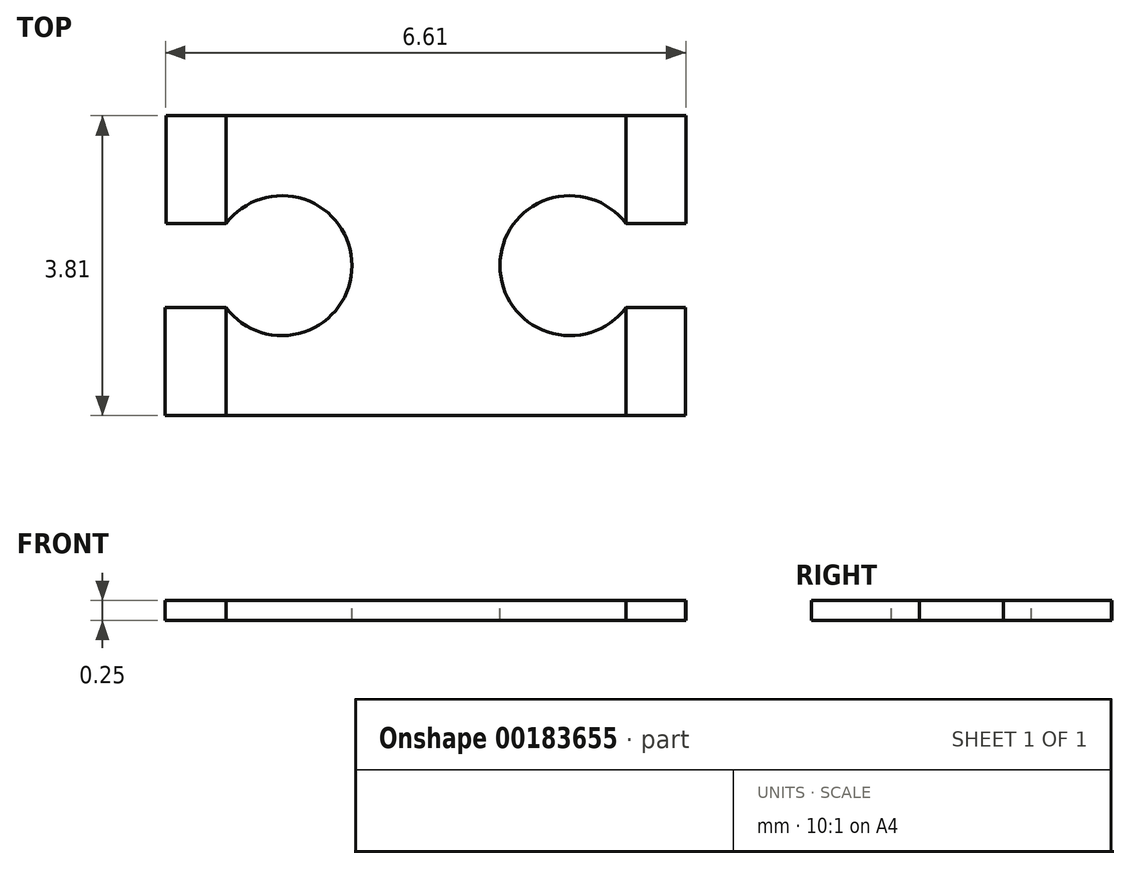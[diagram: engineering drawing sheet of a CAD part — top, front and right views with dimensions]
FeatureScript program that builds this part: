
annotation { "Feature Type Name" : "Feature", "Feature Type Description" : "" }
export const myFeature = defineFeature(function(context is Context, id is Id, definition is map)
    precondition{}
    {
        {
            var Q0;
            Q0=qCreatedBy(makeId("Top.planeOp"),FACE);
            var sketch = newSketch(context, id + "F0", { "sketchPlane" : qUnion([Q0])});
            skLineSegment(sketch, "E0.bottom", {"start": v(0, 0) * mm, "end": v(-5.08, 0) * mm});
            skLineSegment(sketch, "E0.top", {"start": v(0, 3.8) * mm, "end": v(-5.08, 3.8) * mm});
            skLineSegment(sketch, "E0.left", {"start": v(0, 0) * mm, "end": v(0, 3.8) * mm});
            skLineSegment(sketch, "E0.right", {"start": v(-5.08, 0) * mm, "end": v(-5.08, 3.8) * mm});
            skSolve(sketch);
        }
        {
            var Q0;
            Q0 = qSketchRegion(id + "F0", true);
            var Q1;
            Q1 = qSketchRegion(id + "F2", true);
            extrude(context, id + "F1", {"entities" : qUnion([Q0, Q1]), "depth" : 0.25 * mm});
        }
        {
            var Q0;
            Q0=makeQuery(id+"F1.opExtrude","CAP_FACE",FACE,{"disambiguationData":[OSD([sQuery(id+"F0.wireOp",EDGE,"E0.bottom"),sQuery(id+"F0.wireOp",EDGE,"E0.top"),sQuery(id+"F0.wireOp",EDGE,"E0.left"),sQuery(id+"F0.wireOp",EDGE,"E0.right")])],"isStart":false});
            var sketch = newSketch(context, id + "F2", { "sketchPlane" : qUnion([Q0])});
            skLineSegment(sketch, "E1", {"start": v(-5.08, 1.9) * mm, "end": v(-4.37, 1.9) * mm});
            skSolve(sketch);
        }
        {
            var Q0;
            Q0=sQuery(id+"F2.wireOp",VERTEX,"E1.end");
            var Q1;
            Q1=makeQuery(id+"F1.opExtrude","SWEPT_BODY",BODY,{"disambiguationData":[OSD([sQuery(id+"F0.wireOp",EDGE,"E0.bottom"),sQuery(id+"F0.wireOp",EDGE,"E0.top"),sQuery(id+"F0.wireOp",EDGE,"E0.left"),sQuery(id+"F0.wireOp",EDGE,"E0.right")])]});
            hole(context, id + "F3", {"style" : HoleStyle.SIMPLE, "endStyle" : HoleEndStyle.BLIND, "holeDiameter" : 1.78 * mm, "holeDepth" : 25.4 * mm, "locations" : qUnion([Q0]), "scope" : qUnion([Q1])});
        }
        {
            var Q0;
            Q0=makeQuery(id+"F1.opExtrude","CAP_FACE",FACE,{"disambiguationData":[OSD([sQuery(id+"F0.wireOp",EDGE,"E0.bottom"),sQuery(id+"F0.wireOp",EDGE,"E0.top"),sQuery(id+"F0.wireOp",EDGE,"E0.left"),sQuery(id+"F0.wireOp",EDGE,"E0.right")])],"isStart":false});
            var sketch = newSketch(context, id + "F4", { "sketchPlane" : qUnion([Q0])});
            skLineSegment(sketch, "E2", {"start": v(0, 1.9) * mm, "end": v(-0.71, 1.9) * mm});
            skSolve(sketch);
        }
        {
            var Q0;
            Q0=sQuery(id+"F4.wireOp",VERTEX,"E2.end");
            var Q1;
            Q1=makeQuery(id+"F1.opExtrude","SWEPT_BODY",BODY,{"disambiguationData":[OSD([sQuery(id+"F0.wireOp",EDGE,"E0.bottom"),sQuery(id+"F0.wireOp",EDGE,"E0.top"),sQuery(id+"F0.wireOp",EDGE,"E0.left"),sQuery(id+"F0.wireOp",EDGE,"E0.right")])]});
            hole(context, id + "F5", {"style" : HoleStyle.SIMPLE, "endStyle" : HoleEndStyle.BLIND, "holeDiameter" : 1.78 * mm, "holeDepth" : 25.4 * mm, "locations" : qUnion([Q0]), "scope" : qUnion([Q1])});
        }
        {
            var Q0;
            Q0=makeQuery(id+"F1.opExtrude","CAP_FACE",FACE,{"disambiguationData":[OSD([sQuery(id+"F0.wireOp",EDGE,"E0.bottom"),sQuery(id+"F0.wireOp",EDGE,"E0.top"),sQuery(id+"F0.wireOp",EDGE,"E0.left"),sQuery(id+"F0.wireOp",EDGE,"E0.right")])],"isStart":false});
            var sketch = newSketch(context, id + "F6", { "sketchPlane" : qUnion([Q0])});
            skLineSegment(sketch, "E3", {"start": v(-5.08, 2.44) * mm, "end": v(-5.84, 2.44) * mm});
            skLineSegment(sketch, "E4", {"start": v(-5.08, 3.8) * mm, "end": v(-5.84, 3.8) * mm});
            skLineSegment(sketch, "E5", {"start": v(-5.84, 3.8) * mm, "end": v(-5.84, 2.44) * mm});
            skLineSegment(sketch, "E6", {"start": v(-5.08, 1.37) * mm, "end": v(-5.84, 1.37) * mm});
            skLineSegment(sketch, "E7", {"start": v(-5.84, 1.37) * mm, "end": v(-5.84, 0) * mm});
            skLineSegment(sketch, "E8", {"start": v(-5.84, 0) * mm, "end": v(-5.08, 0) * mm});
            skLineSegment(sketch, "E9", {"start": v(0, 2.44) * mm, "end": v(0.76, 2.44) * mm});
            skLineSegment(sketch, "E10", {"start": v(0, 3.8) * mm, "end": v(0.76, 3.8) * mm});
            skLineSegment(sketch, "E11", {"start": v(0.76, 3.8) * mm, "end": v(0.76, 2.44) * mm});
            skLineSegment(sketch, "E12", {"start": v(0, 1.37) * mm, "end": v(0.76, 1.37) * mm});
            skLineSegment(sketch, "E13", {"start": v(0.76, 1.37) * mm, "end": v(0.76, 0) * mm});
            skLineSegment(sketch, "E14", {"start": v(0.76, 0) * mm, "end": v(0, 0) * mm});
            skSolve(sketch);
        }
        {
            var Q0;
            Q0=makeQuery(id+"F6.imprint","IMPRINT",FACE,{"disambiguationData":[TD([[makeQuery(id+"F6.imprint","IMPRINT",EDGE,{"derivedFrom":sQuery(id+"F6.wireOp",EDGE,"E9")}),1.0]])]});
            extrude(context, id + "F7", {"entities" : qUnion([Q0]), "oppositeDirection" : true, "depth" : 0.25 * mm});
        }
        {
            var Q0;
            Q0=makeQuery(id+"F1.opExtrude","CAP_FACE",FACE,{"disambiguationData":[OSD([sQuery(id+"F0.wireOp",EDGE,"E0.bottom"),sQuery(id+"F0.wireOp",EDGE,"E0.top"),sQuery(id+"F0.wireOp",EDGE,"E0.left"),sQuery(id+"F0.wireOp",EDGE,"E0.right")])],"isStart":false});
            var sketch = newSketch(context, id + "F8", { "sketchPlane" : qUnion([Q0])});
            skLineSegment(sketch, "E15", {"start": v(-5.08, 2.44) * mm, "end": v(-5.84, 2.44) * mm});
            skLineSegment(sketch, "E16", {"start": v(-5.84, 2.44) * mm, "end": v(-5.84, 3.81) * mm});
            skLineSegment(sketch, "E17", {"start": v(-5.84, 3.81) * mm, "end": v(-5.08, 3.8) * mm});
            skSolve(sketch);
        }
        {
            var Q0;
            Q0=makeQuery(id+"F8.imprint","IMPRINT",FACE,{"disambiguationData":[TD([[makeQuery(id+"F8.imprint","IMPRINT",EDGE,{"derivedFrom":sQuery(id+"F8.wireOp",EDGE,"E15")}),-1.0]])]});
            extrude(context, id + "F9", {"entities" : qUnion([Q0]), "oppositeDirection" : true, "depth" : 0.25 * mm});
        }
        {
            var Q0;
            Q0=makeQuery(id+"F1.opExtrude","CAP_FACE",FACE,{"disambiguationData":[OSD([sQuery(id+"F0.wireOp",EDGE,"E0.bottom"),sQuery(id+"F0.wireOp",EDGE,"E0.top"),sQuery(id+"F0.wireOp",EDGE,"E0.left"),sQuery(id+"F0.wireOp",EDGE,"E0.right")])],"isStart":false});
            var sketch = newSketch(context, id + "F10", { "sketchPlane" : qUnion([Q0])});
            skLineSegment(sketch, "E18", {"start": v(0, 1.37) * mm, "end": v(0.76, 1.37) * mm});
            skLineSegment(sketch, "E19", {"start": v(0.76, 1.37) * mm, "end": v(0.76, 0) * mm});
            skLineSegment(sketch, "E20", {"start": v(0.76, 0) * mm, "end": v(0, 0) * mm});
            skSolve(sketch);
        }
        {
            var Q0;
            Q0=makeQuery(id+"F10.imprint","IMPRINT",FACE,{"disambiguationData":[TD([[makeQuery(id+"F10.imprint","IMPRINT",EDGE,{"derivedFrom":sQuery(id+"F10.wireOp",EDGE,"E18")}),-1.0]])]});
            extrude(context, id + "F11", {"entities" : qUnion([Q0]), "oppositeDirection" : true, "depth" : 0.25 * mm});
        }
        {
            var Q0;
            Q0=makeQuery(id+"F1.opExtrude","CAP_FACE",FACE,{"disambiguationData":[OSD([sQuery(id+"F0.wireOp",EDGE,"E0.bottom"),sQuery(id+"F0.wireOp",EDGE,"E0.top"),sQuery(id+"F0.wireOp",EDGE,"E0.left"),sQuery(id+"F0.wireOp",EDGE,"E0.right")])],"isStart":false});
            var sketch = newSketch(context, id + "F12", { "sketchPlane" : qUnion([Q0])});
            skLineSegment(sketch, "E21", {"start": v(-5.08, 1.37) * mm, "end": v(-5.85, 1.37) * mm});
            skLineSegment(sketch, "E22", {"start": v(-5.85, 1.37) * mm, "end": v(-5.85, 0) * mm});
            skLineSegment(sketch, "E23", {"start": v(-5.85, 0) * mm, "end": v(-5.08, 0) * mm});
            skSolve(sketch);
        }
        {
            var Q0;
            Q0=makeQuery(id+"F12.imprint","IMPRINT",FACE,{"disambiguationData":[TD([[makeQuery(id+"F12.imprint","IMPRINT",EDGE,{"derivedFrom":sQuery(id+"F12.wireOp",EDGE,"E21")}),1.0]])]});
            extrude(context, id + "F13", {"entities" : qUnion([Q0]), "oppositeDirection" : true, "depth" : 0.25 * mm});
        }
    });
